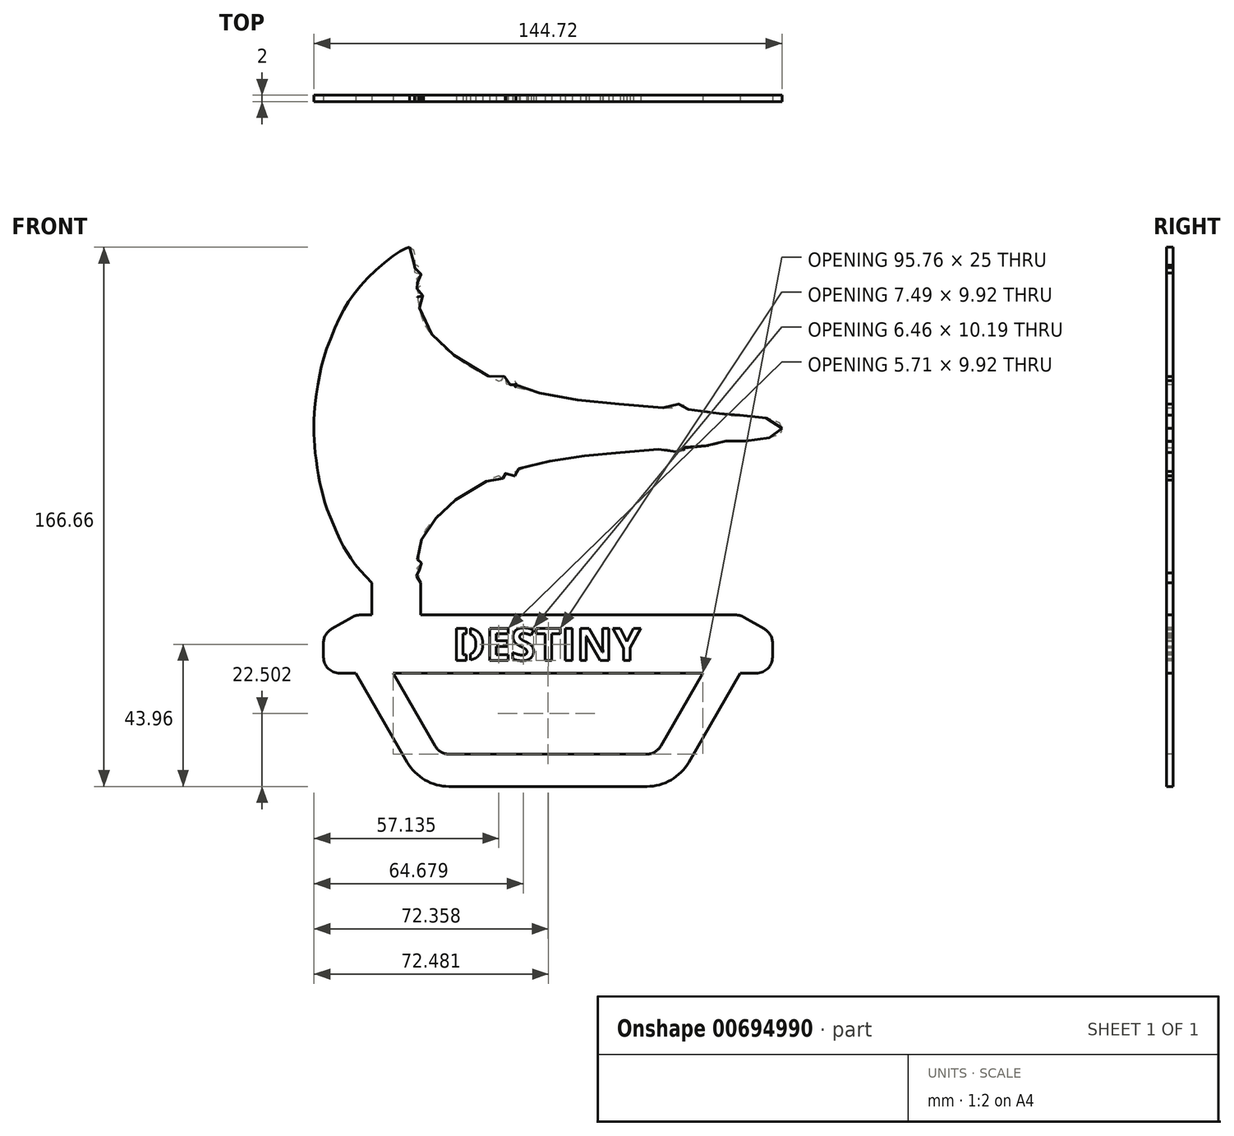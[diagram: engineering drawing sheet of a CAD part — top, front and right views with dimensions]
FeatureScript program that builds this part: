
annotation { "Feature Type Name" : "Feature", "Feature Type Description" : "" }
export const myFeature = defineFeature(function(context is Context, id is Id, definition is map)
    precondition{}
    {
        {
            var Q0;
            Q0=qCreatedBy(makeId("Front.planeOp"),FACE);
            var sketch = newSketch(context, id + "F0", { "sketchPlane" : qUnion([Q0])});
            skFitSpline(sketch, "E0", {"points": [v(-25.66, 55.94) * mm, v(-27.34, 55.41) * mm, v(-34.33, 50.4) * mm, v(-42.76, 41.67) * mm, v(-47.27, 34.16) * mm, v(-51.71, 23.26) * mm, v(-53.61, 15.5) * mm, v(-54.95, 6.33) * mm, v(-55.2, 0) * mm], "startDerivative": vector(-24.5, -4.74) * mm, "endDerivative": vector(-0.49, -53.24) * mm});
            skLineSegment(sketch, "E1", {"start": v(-55.2, 0) * mm, "end": v(0, 0) * mm, "construction": true});
            skFitSpline(sketch, "E2", {"points": [v(-25.66, 55.94) * mm, v(-24.59, 55.32) * mm, v(-24.1, 53.88) * mm, v(-24.2, 51.55) * mm, v(-24.17, 50.7) * mm, v(-23.7, 50.4) * mm, v(-23.23, 50.38) * mm, v(-22.81, 50.11) * mm, v(-22.78, 49.77) * mm, v(-23.25, 49.64) * mm, v(-23.8, 49.62) * mm, v(-24.12, 49.3) * mm, v(-24.2, 48.8) * mm, v(-24.17, 48.28) * mm, v(-24.17, 48) * mm, v(-23.23, 47.94) * mm, v(-22.6, 47.81) * mm, v(-21.9, 47.52) * mm, v(-21.87, 47.16) * mm, v(-22.57, 46.84) * mm, v(-23.3, 46.71) * mm, v(-23.52, 45.9) * mm, v(-23.23, 44.88) * mm, v(-22.68, 44.75) * mm, v(-21.9, 44.57) * mm, v(-21.84, 44) * mm, v(-22.63, 43.73) * mm, v(-23.2, 43.57) * mm, v(-23.4, 42.7) * mm, v(-23.17, 42) * mm, v(-22.43, 41.8) * mm, v(-21.79, 41.67) * mm, v(-21.35, 41.54) * mm, v(-21.37, 41.1) * mm, v(-21.79, 40.95) * mm, v(-22.47, 40.7) * mm, v(-23.17, 40.57) * mm, v(-23.17, 40.02) * mm, v(-22.8, 38) * mm, v(-21.87, 34.35) * mm, v(-20.32, 30.8) * mm, v(-17.58, 27.81) * mm, v(-15.3, 25.33) * mm, v(-11.25, 22.08) * mm, v(-4.9, 17.85) * mm, v(0.88, 15.11) * mm, v(2.56, 14.47) * mm, v(2.84, 15.06) * mm, v(3.4, 15.79) * mm, v(3.68, 15.97) * mm, v(4, 15.86) * mm, v(4.1, 15.48) * mm, v(4.03, 14.62) * mm, v(3.96, 14.12) * mm, v(4.7, 13.54) * mm, v(5.75, 13.48) * mm, v(5.97, 13.92) * mm, v(6.39, 14.43) * mm, v(6.8, 14.76) * mm, v(7.18, 14.62) * mm, v(7.22, 14.03) * mm, v(7.13, 13.4) * mm, v(7.07, 12.84) * mm, v(7.84, 12.55) * mm, v(13.21, 11.2) * mm, v(19.06, 9.9) * mm, v(26.24, 8.8) * mm, v(34.86, 7.83) * mm, v(41.1, 7.35) * mm, v(49.95, 6.64) * mm, v(56.13, 6.18) * mm, v(56.36, 6.29) * mm, v(56.58, 6.77) * mm, v(56.81, 7.35) * mm, v(57.1, 7.5) * mm, v(58.68, 7.4) * mm, v(59.07, 7.19) * mm, v(59.2, 6.55) * mm, v(59.32, 6.08) * mm, v(59.57, 5.88) * mm, v(60.4, 5.82) * mm, v(65, 5.52) * mm, v(69.13, 4.9) * mm, v(71.56, 3.96) * mm, v(72.18, 3.96) * mm, v(74.17, 3.88) * mm, v(76.73, 4.03) * mm, v(79.16, 3.79) * mm, v(83.05, 3.37) * mm, v(86.16, 2.78) * mm, v(88.43, 1.9) * mm, v(89.3, 1.25) * mm, v(89.52, 0) * mm], "startDerivative": vector(114.52, -46.4) * mm, "endDerivative": vector(5.46, -132.34) * mm});
            skFitSpline(sketch, "E3.MirrorCS", {"points": [v(-25.66, -55.94) * mm, v(-24.59, -55.32) * mm, v(-24.1, -53.88) * mm, v(-24.2, -51.55) * mm, v(-24.17, -50.7) * mm, v(-23.7, -50.4) * mm, v(-23.23, -50.38) * mm, v(-22.81, -50.11) * mm, v(-22.78, -49.77) * mm, v(-23.25, -49.64) * mm, v(-23.8, -49.62) * mm, v(-24.12, -49.3) * mm, v(-24.2, -48.8) * mm, v(-24.17, -48.28) * mm, v(-24.17, -48) * mm, v(-23.23, -47.94) * mm, v(-22.6, -47.81) * mm, v(-21.9, -47.52) * mm, v(-21.87, -47.16) * mm, v(-22.57, -46.84) * mm, v(-23.3, -46.71) * mm, v(-23.52, -45.9) * mm, v(-23.23, -44.88) * mm, v(-22.68, -44.75) * mm, v(-21.9, -44.57) * mm, v(-21.84, -44) * mm, v(-22.63, -43.73) * mm, v(-23.2, -43.57) * mm, v(-23.4, -42.7) * mm, v(-23.17, -42) * mm, v(-22.43, -41.8) * mm, v(-21.79, -41.67) * mm, v(-21.35, -41.54) * mm, v(-21.37, -41.1) * mm, v(-21.79, -40.95) * mm, v(-22.47, -40.7) * mm, v(-23.17, -40.57) * mm, v(-23.17, -40.02) * mm, v(-22.8, -38) * mm, v(-21.87, -34.35) * mm, v(-20.32, -30.8) * mm, v(-17.58, -27.81) * mm, v(-15.3, -25.33) * mm, v(-11.25, -22.08) * mm, v(-4.9, -17.85) * mm, v(0.88, -15.11) * mm, v(2.56, -14.47) * mm, v(2.84, -15.06) * mm, v(3.4, -15.79) * mm, v(3.68, -15.97) * mm, v(4, -15.86) * mm, v(4.1, -15.48) * mm, v(4.03, -14.62) * mm, v(3.96, -14.12) * mm, v(4.7, -13.54) * mm, v(5.75, -13.48) * mm, v(5.97, -13.92) * mm, v(6.39, -14.43) * mm, v(6.8, -14.76) * mm, v(7.18, -14.62) * mm, v(7.22, -14.03) * mm, v(7.13, -13.4) * mm, v(7.07, -12.84) * mm, v(7.84, -12.55) * mm, v(13.21, -11.2) * mm, v(19.06, -9.9) * mm, v(26.24, -8.8) * mm, v(34.86, -7.83) * mm, v(41.1, -7.35) * mm, v(49.95, -6.64) * mm, v(56.13, -6.18) * mm, v(56.36, -6.29) * mm, v(56.58, -6.77) * mm, v(56.81, -7.35) * mm, v(57.1, -7.5) * mm, v(58.68, -7.4) * mm, v(59.07, -7.19) * mm, v(59.2, -6.55) * mm, v(59.32, -6.08) * mm, v(59.57, -5.88) * mm, v(60.4, -5.82) * mm, v(65, -5.52) * mm, v(69.13, -4.9) * mm, v(71.56, -3.96) * mm, v(72.18, -3.96) * mm, v(74.17, -3.88) * mm, v(76.73, -4.03) * mm, v(79.16, -3.79) * mm, v(83.05, -3.37) * mm, v(86.16, -2.78) * mm, v(88.43, -1.9) * mm, v(89.3, -1.25) * mm, v(89.52, 0) * mm], "startDerivative": vector(114.52, 46.4) * mm, "endDerivative": vector(5.46, 132.34) * mm});
            skFitSpline(sketch, "E4.MirrorCS", {"points": [v(-25.66, -55.94) * mm, v(-27.34, -55.41) * mm, v(-34.33, -50.4) * mm, v(-42.76, -41.67) * mm, v(-47.27, -34.16) * mm, v(-51.71, -23.26) * mm, v(-53.61, -15.5) * mm, v(-54.95, -6.33) * mm, v(-55.2, 0) * mm], "startDerivative": vector(-24.5, 4.74) * mm, "endDerivative": vector(-0.49, 53.24) * mm});
            skSolve(sketch);
        }
        {
            var Q0;
            Q0 = qSketchRegion(id + "F0", true);
            extrude(context, id + "F1", {"entities" : qUnion([Q0]), "depth" : 2 * mm, "offsetDistance" : 25 * mm});
        }
        {
            var Q0;
            Q0=makeQuery(id+"F1.opExtrude","CAP_FACE",FACE,{"disambiguationData":[OSD([sQuery(id+"F0.wireOp",EDGE,"E0"),sQuery(id+"F0.wireOp",EDGE,"E2"),sQuery(id+"F0.wireOp",EDGE,"E3.MirrorCS"),sQuery(id+"F0.wireOp",EDGE,"E4.MirrorCS")])],"isStart":false});
            var sketch = newSketch(context, id + "F2", { "sketchPlane" : qUnion([Q0])});
            skLineSegment(sketch, "E5.bottom", {"start": v(-22.27, -47.72) * mm, "end": v(-37.27, -47.72) * mm});
            skLineSegment(sketch, "E5.top", {"start": v(-22.27, -57.72) * mm, "end": v(-37.27, -57.72) * mm});
            skLineSegment(sketch, "E5.left", {"start": v(-22.27, -47.72) * mm, "end": v(-22.27, -57.72) * mm});
            skLineSegment(sketch, "E5.right", {"start": v(-37.27, -47.72) * mm, "end": v(-37.27, -57.72) * mm});
            skLineSegment(sketch, "E6", {"start": v(-37.27, -57.72) * mm, "end": v(-42.27, -57.72) * mm});
            skLineSegment(sketch, "E7", {"start": v(-52.27, -63.5) * mm, "end": v(-42.27, -57.72) * mm});
            skLineSegment(sketch, "E8", {"start": v(-52.27, -63.5) * mm, "end": v(-52.27, -75.72) * mm});
            skLineSegment(sketch, "E9", {"start": v(-52.27, -75.72) * mm, "end": v(86.58, -75.72) * mm});
            skLineSegment(sketch, "E10", {"start": v(86.58, -75.72) * mm, "end": v(86.58, -63.5) * mm});
            skLineSegment(sketch, "E11", {"start": v(76.58, -57.72) * mm, "end": v(86.58, -63.5) * mm});
            skLineSegment(sketch, "E12", {"start": v(76.58, -57.72) * mm, "end": v(-22.27, -57.72) * mm});
            skLineSegment(sketch, "E13", {"start": v(-55.2, 0) * mm, "end": v(89.52, 0) * mm, "construction": true});
            skLineSegment(sketch, "E14", {"start": v(17.16, 0) * mm, "end": v(17.16, -57.72) * mm, "construction": true});
            skText(sketch, "E15", { "text": "DESTINY", "fontName": "OpenSans-Bold.ttf"});
            skLineSegment(sketch, "E16", {"start": v(-42.27, -75.72) * mm, "end": v(-22.06, -110.72) * mm});
            skLineSegment(sketch, "E17", {"start": v(-22.06, -110.72) * mm, "end": v(56.38, -110.72) * mm});
            skLineSegment(sketch, "E18", {"start": v(56.38, -110.72) * mm, "end": v(76.58, -75.72) * mm});
            skLineSegment(sketch, "E19.0", {"start": v(50.6, -100.72) * mm, "end": v(65.04, -75.72) * mm});
            skLineSegment(sketch, "E19.1", {"start": v(-16.29, -100.72) * mm, "end": v(50.6, -100.72) * mm});
            skLineSegment(sketch, "E19.2", {"start": v(-30.72, -75.72) * mm, "end": v(-16.29, -100.72) * mm});
            const initialGuessF2  = {"E15": [-0.01245, -0.07172, 1, 0, 0.01]};
            skSetInitialGuess(sketch, initialGuessF2);
            skSolve(sketch);
        }
        {
            var Q0;
            {var subQ0=sQuery(id+"F2.wireOp",EDGE,"E16");Q0=makeQuery(id+"F2.imprint","IMPRINT",FACE,{"disambiguationData":[TD([[makeQuery(id+"F2.imprint","IMPRINT",EDGE,{"derivedFrom":subQ0}),1.0]])]});}
            var Q1;
            {var subQ0=sQuery(id+"F2.wireOp",EDGE,"E5.bottom");Q1=makeQuery(id+"F2.imprint","IMPRINT",FACE,{"disambiguationData":[TD([[makeQuery(id+"F2.imprint","IMPRINT",EDGE,{"derivedFrom":subQ0}),1.0]])]});}
            var Q2;
            Q2=makeQuery(id+"F2.imprint","IMPRINT",FACE,{"disambiguationData":[TD([[makeQuery(id+"F2.imprint","IMPRINT",EDGE,{"derivedFrom":sQuery(id+"F2.wireOp",EDGE,"E5.top")}),-1.0]])]});
            var Q3;
            Q3=makeQuery(id+"F2.imprint","IMPRINT",FACE,{"disambiguationData":[TD([[makeQuery(id+"F2.imprint","IMPRINT",EDGE,{"derivedFrom":sQuery(id+"F2.wireOp",EDGE,"E15.sketch_text.stroke-7")}),1.0]])]});
            var Q4;
            Q4=makeQuery(id+"F2.imprint","IMPRINT",FACE,{"disambiguationData":[TD([[makeQuery(id+"F2.imprint","IMPRINT",EDGE,{"derivedFrom":sQuery(id+"F2.wireOp",EDGE,"E5.top")}),1.0]])]});
            var Q5;
            Q5=makeQuery(id+"F1.opExtrude","CAP_FACE",FACE,{"disambiguationData":[OSD([sQuery(id+"F0.wireOp",EDGE,"E0"),sQuery(id+"F0.wireOp",EDGE,"E2"),sQuery(id+"F0.wireOp",EDGE,"E3.MirrorCS"),sQuery(id+"F0.wireOp",EDGE,"E4.MirrorCS")])],"isStart":true});
            extrude(context, id + "F3", {"entities" : qUnion([Q0, Q1, Q2, Q3, Q4]), "operationType" : NewBodyOperationType.ADD, "endBound" : BoundingType.UP_TO_SURFACE, "oppositeDirection" : true, "depth" : 25 * mm, "endBoundEntityFace" : qUnion([Q5]), "offsetDistance" : 25 * mm});
        }
        {
            var Q0;
            Q0=makeQuery(id+"F3.boolean.opBoolean","MERGE",FACE,{"derivedFrom":[makeQuery(id+"F1.opExtrude","CAP_FACE",FACE,{"disambiguationData":[OSD([sQuery(id+"F0.wireOp",EDGE,"E0"),sQuery(id+"F0.wireOp",EDGE,"E2"),sQuery(id+"F0.wireOp",EDGE,"E3.MirrorCS"),sQuery(id+"F0.wireOp",EDGE,"E4.MirrorCS")])],"isStart":false}),makeQuery(id+"F3.opExtrude","CAP_FACE",FACE,{"disambiguationData":[OSD([sQuery(id+"F2.wireOp",EDGE,"E5.bottom"),sQuery(id+"F2.wireOp",EDGE,"E5.left"),sQuery(id+"F2.wireOp",EDGE,"E5.right"),sQuery(id+"F2.wireOp",EDGE,"E6"),sQuery(id+"F2.wireOp",EDGE,"E7"),sQuery(id+"F2.wireOp",EDGE,"E8"),sQuery(id+"F2.wireOp",EDGE,"E9"),sQuery(id+"F2.wireOp",EDGE,"E10"),sQuery(id+"F2.wireOp",EDGE,"E11"),sQuery(id+"F2.wireOp",EDGE,"E12"),sQuery(id+"F2.wireOp",EDGE,"E15.sketch_text.stroke-0"),sQuery(id+"F2.wireOp",EDGE,"E15.sketch_text.stroke-1"),sQuery(id+"F2.wireOp",EDGE,"E15.sketch_text.stroke-2"),sQuery(id+"F2.wireOp",EDGE,"E15.sketch_text.stroke-3"),sQuery(id+"F2.wireOp",EDGE,"E15.sketch_text.stroke-4"),sQuery(id+"F2.wireOp",EDGE,"E15.sketch_text.stroke-5"),sQuery(id+"F2.wireOp",EDGE,"E15.sketch_text.stroke-6"),sQuery(id+"F2.wireOp",EDGE,"E15.sketch_text.stroke-12"),sQuery(id+"F2.wireOp",EDGE,"E15.sketch_text.stroke-13"),sQuery(id+"F2.wireOp",EDGE,"E15.sketch_text.stroke-14"),sQuery(id+"F2.wireOp",EDGE,"E15.sketch_text.stroke-15"),sQuery(id+"F2.wireOp",EDGE,"E15.sketch_text.stroke-16"),sQuery(id+"F2.wireOp",EDGE,"E15.sketch_text.stroke-17"),sQuery(id+"F2.wireOp",EDGE,"E15.sketch_text.stroke-18"),sQuery(id+"F2.wireOp",EDGE,"E15.sketch_text.stroke-19"),sQuery(id+"F2.wireOp",EDGE,"E15.sketch_text.stroke-20"),sQuery(id+"F2.wireOp",EDGE,"E15.sketch_text.stroke-21"),sQuery(id+"F2.wireOp",EDGE,"E15.sketch_text.stroke-22"),sQuery(id+"F2.wireOp",EDGE,"E15.sketch_text.stroke-23"),sQuery(id+"F2.wireOp",EDGE,"E15.sketch_text.stroke-24"),sQuery(id+"F2.wireOp",EDGE,"E15.sketch_text.stroke-25"),sQuery(id+"F2.wireOp",EDGE,"E15.sketch_text.stroke-26"),sQuery(id+"F2.wireOp",EDGE,"E15.sketch_text.stroke-27"),sQuery(id+"F2.wireOp",EDGE,"E15.sketch_text.stroke-28"),sQuery(id+"F2.wireOp",EDGE,"E15.sketch_text.stroke-29"),sQuery(id+"F2.wireOp",EDGE,"E15.sketch_text.stroke-30"),sQuery(id+"F2.wireOp",EDGE,"E15.sketch_text.stroke-31"),sQuery(id+"F2.wireOp",EDGE,"E15.sketch_text.stroke-32"),sQuery(id+"F2.wireOp",EDGE,"E15.sketch_text.stroke-33"),sQuery(id+"F2.wireOp",EDGE,"E15.sketch_text.stroke-34"),sQuery(id+"F2.wireOp",EDGE,"E15.sketch_text.stroke-35"),sQuery(id+"F2.wireOp",EDGE,"E15.sketch_text.stroke-36"),sQuery(id+"F2.wireOp",EDGE,"E15.sketch_text.stroke-37"),sQuery(id+"F2.wireOp",EDGE,"E15.sketch_text.stroke-38"),sQuery(id+"F2.wireOp",EDGE,"E15.sketch_text.stroke-39"),sQuery(id+"F2.wireOp",EDGE,"E15.sketch_text.stroke-40"),sQuery(id+"F2.wireOp",EDGE,"E15.sketch_text.stroke-41"),sQuery(id+"F2.wireOp",EDGE,"E15.sketch_text.stroke-42"),sQuery(id+"F2.wireOp",EDGE,"E15.sketch_text.stroke-43"),sQuery(id+"F2.wireOp",EDGE,"E15.sketch_text.stroke-44"),sQuery(id+"F2.wireOp",EDGE,"E15.sketch_text.stroke-45"),sQuery(id+"F2.wireOp",EDGE,"E15.sketch_text.stroke-46"),sQuery(id+"F2.wireOp",EDGE,"E15.sketch_text.stroke-47"),sQuery(id+"F2.wireOp",EDGE,"E15.sketch_text.stroke-48"),sQuery(id+"F2.wireOp",EDGE,"E15.sketch_text.stroke-49"),sQuery(id+"F2.wireOp",EDGE,"E15.sketch_text.stroke-50"),sQuery(id+"F2.wireOp",EDGE,"E15.sketch_text.stroke-51"),sQuery(id+"F2.wireOp",EDGE,"E15.sketch_text.stroke-52"),sQuery(id+"F2.wireOp",EDGE,"E15.sketch_text.stroke-53"),sQuery(id+"F2.wireOp",EDGE,"E15.sketch_text.stroke-54"),sQuery(id+"F2.wireOp",EDGE,"E15.sketch_text.stroke-55"),sQuery(id+"F2.wireOp",EDGE,"E15.sketch_text.stroke-56"),sQuery(id+"F2.wireOp",EDGE,"E15.sketch_text.stroke-57"),sQuery(id+"F2.wireOp",EDGE,"E15.sketch_text.stroke-58"),sQuery(id+"F2.wireOp",EDGE,"E15.sketch_text.stroke-59"),sQuery(id+"F2.wireOp",EDGE,"E15.sketch_text.stroke-60"),sQuery(id+"F2.wireOp",EDGE,"E15.sketch_text.stroke-61"),sQuery(id+"F2.wireOp",EDGE,"E15.sketch_text.stroke-62"),sQuery(id+"F2.wireOp",EDGE,"E15.sketch_text.stroke-63"),sQuery(id+"F2.wireOp",EDGE,"E15.sketch_text.stroke-64"),sQuery(id+"F2.wireOp",EDGE,"E15.sketch_text.stroke-65"),sQuery(id+"F2.wireOp",EDGE,"E15.sketch_text.stroke-66"),sQuery(id+"F2.wireOp",EDGE,"E15.sketch_text.stroke-67"),sQuery(id+"F2.wireOp",EDGE,"E15.sketch_text.stroke-68"),sQuery(id+"F2.wireOp",EDGE,"E15.sketch_text.stroke-69"),sQuery(id+"F2.wireOp",EDGE,"E15.sketch_text.stroke-70"),sQuery(id+"F2.wireOp",EDGE,"E15.sketch_text.stroke-71"),sQuery(id+"F2.wireOp",EDGE,"E15.sketch_text.stroke-72"),sQuery(id+"F2.wireOp",EDGE,"E15.sketch_text.stroke-73"),sQuery(id+"F2.wireOp",EDGE,"E15.sketch_text.stroke-74"),sQuery(id+"F2.wireOp",EDGE,"E15.sketch_text.stroke-75"),sQuery(id+"F2.wireOp",EDGE,"E15.sketch_text.stroke-76"),sQuery(id+"F2.wireOp",EDGE,"E15.sketch_text.stroke-77"),sQuery(id+"F2.wireOp",EDGE,"E15.sketch_text.stroke-78"),sQuery(id+"F2.wireOp",EDGE,"E15.sketch_text.stroke-79"),sQuery(id+"F2.wireOp",EDGE,"E15.sketch_text.stroke-80"),sQuery(id+"F2.wireOp",EDGE,"E15.sketch_text.stroke-81"),sQuery(id+"F2.wireOp",EDGE,"E15.sketch_text.stroke-82"),sQuery(id+"F2.wireOp",EDGE,"E15.sketch_text.stroke-83"),sQuery(id+"F2.wireOp",EDGE,"E15.sketch_text.stroke-84"),sQuery(id+"F2.wireOp",EDGE,"E15.sketch_text.stroke-85"),sQuery(id+"F2.wireOp",EDGE,"E15.sketch_text.stroke-86"),sQuery(id+"F2.wireOp",EDGE,"E16"),sQuery(id+"F2.wireOp",EDGE,"E17"),sQuery(id+"F2.wireOp",EDGE,"E18"),sQuery(id+"F2.wireOp",EDGE,"E19.0"),sQuery(id+"F2.wireOp",EDGE,"E19.1"),sQuery(id+"F2.wireOp",EDGE,"E19.2")])],"isStart":true})]});
            var sketch = newSketch(context, id + "F4", { "sketchPlane" : qUnion([Q0])});
            skLineSegment(sketch, "E20.bottom", {"start": v(-8.09, -61.8) * mm, "end": v(-6.89, -61.8) * mm});
            skLineSegment(sketch, "E20.top", {"start": v(-8.09, -71.72) * mm, "end": v(-6.89, -71.72) * mm});
            skLineSegment(sketch, "E20.left", {"start": v(-8.09, -61.8) * mm, "end": v(-8.09, -71.72) * mm});
            skLineSegment(sketch, "E20.right", {"start": v(-6.89, -61.8) * mm, "end": v(-6.89, -71.72) * mm});
            skSolve(sketch);
        }
        {
            var Q0;
            {var subQ1=makeQuery(id+"F3.opExtrude","CAP_EDGE",EDGE,{"disambiguationData":[OSD([sQuery(id+"F2.wireOp",EDGE,"E15.sketch_text.stroke-5")])],"isStart":true});var subQ5=sQuery(id+"F4.wireOp",EDGE,"E20.right");var subQ6=makeQuery(id+"F4.imprint","INTERSECT",VERTEX,{"derivedFrom":[subQ1,subQ5]});Q0=makeQuery(id+"F4.imprint","IMPRINT",FACE,{"disambiguationData":[TD([[makeQuery(id+"F4.imprint","IMPRINT",EDGE,{"disambiguationData":[TD([[subQ6,-1.0]])],"derivedFrom":subQ5}),-1.0]])]});}
            var Q1;
            {var subQ0=sQuery(id+"F0.wireOp",EDGE,"E4.MirrorCS");var subQ1=sQuery(id+"F0.wireOp",EDGE,"E3.MirrorCS");var subQ2=sQuery(id+"F0.wireOp",EDGE,"E2");var subQ3=sQuery(id+"F0.wireOp",EDGE,"E0");Q1=makeQuery(id+"F3.boolean.opBoolean","MERGE",FACE,{"derivedFrom":[makeQuery(id+"F1.opExtrude","CAP_FACE",FACE,{"disambiguationData":[OSD([subQ3,subQ2,subQ1,subQ0])],"isStart":true}),makeQuery(id+"F3.opExtrude","CAP_FACE",FACE,{"disambiguationData":[OSD([subQ3,subQ2,subQ1,subQ0]),OD(0.0)],"isStart":false})]});}
            extrude(context, id + "F5", {"entities" : qUnion([Q0]), "operationType" : NewBodyOperationType.ADD, "endBound" : BoundingType.UP_TO_SURFACE, "oppositeDirection" : true, "depth" : 25 * mm, "endBoundEntityFace" : qUnion([Q1]), "offsetDistance" : 25 * mm});
        }
        {
            var Q0;
            Q0=makeQuery(id+"F3.opExtrude","SWEPT_EDGE",EDGE,{"disambiguationData":[OSD([sQuery(id+"F2.wireOp",EDGE,"E6"),sQuery(id+"F2.wireOp",EDGE,"E7")])]});
            var Q1;
            Q1=makeQuery(id+"F3.opExtrude","SWEPT_EDGE",EDGE,{"disambiguationData":[OSD([sQuery(id+"F2.wireOp",EDGE,"E7"),sQuery(id+"F2.wireOp",EDGE,"E8")])]});
            var Q2;
            Q2=makeQuery(id+"F3.opExtrude","SWEPT_EDGE",EDGE,{"disambiguationData":[OSD([sQuery(id+"F2.wireOp",EDGE,"E8"),sQuery(id+"F2.wireOp",EDGE,"E9")])]});
            var Q3;
            Q3=makeQuery(id+"F3.opExtrude","SWEPT_EDGE",EDGE,{"disambiguationData":[OSD([sQuery(id+"F2.wireOp",EDGE,"E9"),sQuery(id+"F2.wireOp",EDGE,"E10")])]});
            var Q4;
            Q4=makeQuery(id+"F3.opExtrude","SWEPT_EDGE",EDGE,{"disambiguationData":[OSD([sQuery(id+"F2.wireOp",EDGE,"E10"),sQuery(id+"F2.wireOp",EDGE,"E11")])]});
            var Q5;
            Q5=makeQuery(id+"F3.opExtrude","SWEPT_EDGE",EDGE,{"disambiguationData":[OSD([sQuery(id+"F2.wireOp",EDGE,"E11"),sQuery(id+"F2.wireOp",EDGE,"E12")])]});
            var Q6;
            Q6=makeQuery(id+"F3.opExtrude","SWEPT_EDGE",EDGE,{"disambiguationData":[OSD([sQuery(id+"F2.wireOp",EDGE,"E19.0"),sQuery(id+"F2.wireOp",EDGE,"E19.1")])]});
            var Q7;
            Q7=makeQuery(id+"F3.opExtrude","SWEPT_EDGE",EDGE,{"disambiguationData":[OSD([sQuery(id+"F2.wireOp",EDGE,"E19.1"),sQuery(id+"F2.wireOp",EDGE,"E19.2")])]});
            fillet(context, id + "F6", {"entities" : qUnion([Q0, Q1, Q2, Q3, Q4, Q5, Q6, Q7]), "radius" : 5 * mm, "tangentPropagation" : true, "allowEdgeOverflow" : false});
        }
        {
            var Q0;
            Q0=makeQuery(id+"F3.opExtrude","SWEPT_EDGE",EDGE,{"disambiguationData":[OSD([sQuery(id+"F2.wireOp",EDGE,"E16"),sQuery(id+"F2.wireOp",EDGE,"E17")])]});
            var Q1;
            Q1=makeQuery(id+"F3.opExtrude","SWEPT_EDGE",EDGE,{"disambiguationData":[OSD([sQuery(id+"F2.wireOp",EDGE,"E17"),sQuery(id+"F2.wireOp",EDGE,"E18")])]});
            fillet(context, id + "F7", {"entities" : qUnion([Q0, Q1]), "radius" : 15 * mm, "tangentPropagation" : true, "allowEdgeOverflow" : false});
        }
    });
